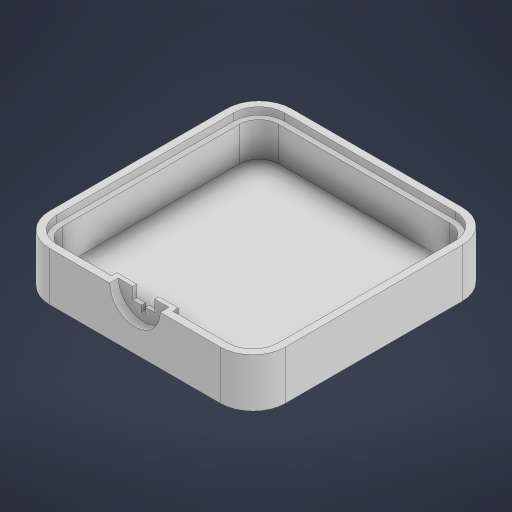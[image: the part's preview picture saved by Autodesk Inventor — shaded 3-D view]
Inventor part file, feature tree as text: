
AUTODESK INVENTOR PART (.ipt)
format: ipt  version: 2024 (Build 280153000, 153)  size: 442,368 bytes
history: native  units: in
note: dims shown in document units (in); Inventor stores cm internally (conversion verified against a paired STEP export)
features: sketch x6, extrude x6, plane x1
ambient origin geometry x8: Origin, YZ Plane, XZ Plane, XY Plane, X Axis, Y Axis, Z Axis, Center Point
bodies: Solid1 (feature_tree)
feature tree (13):
  sketch  "Sketch1"  dims[d3=0.3543in d4=0.3543in]
  extrude  "Extrusion1"  Depth=0.3543in
  extrude  "Extrusion2"  Depth=0.0787in TaperAngle=0.0deg
  extrude  "Extrusion3"  Depth=0.5315in
  extrude  "Extrusion4"  Depth=0.2559in
  plane  "Work Plane1"
  extrude  "Extrusion5"  Depth=0.0197in
  sketch  "Boceto12"  dims[d15=0.0394in d17=0.0197in]
  extrude  "Extrusión11"  Depth=0.0394in
  sketch  "Sketch2"  dims[d5=0.1378in d6=0.0787in d7=0.0in]
  sketch  "Sketch3"  dims[d8=0.5315in d9=0.0in d10=0.5512in]
  sketch  "Sketch5"  dims[d11=0.0945in d12=0.0in d13=0.2559in]
  sketch  "Boceto13"  dims[d18=0.0787in d19=0.0in d20=0.0394in d21=0.0472in d22=0.0in d44=0.0591in d45=0.0783in d46=0.0787in d47=0.0in d48=0.0591in d72=2.2953in d73=2.3622in d75=0.2402in d76=0.0591in d77=0.0in d78=0.0in d79=0.0in]
